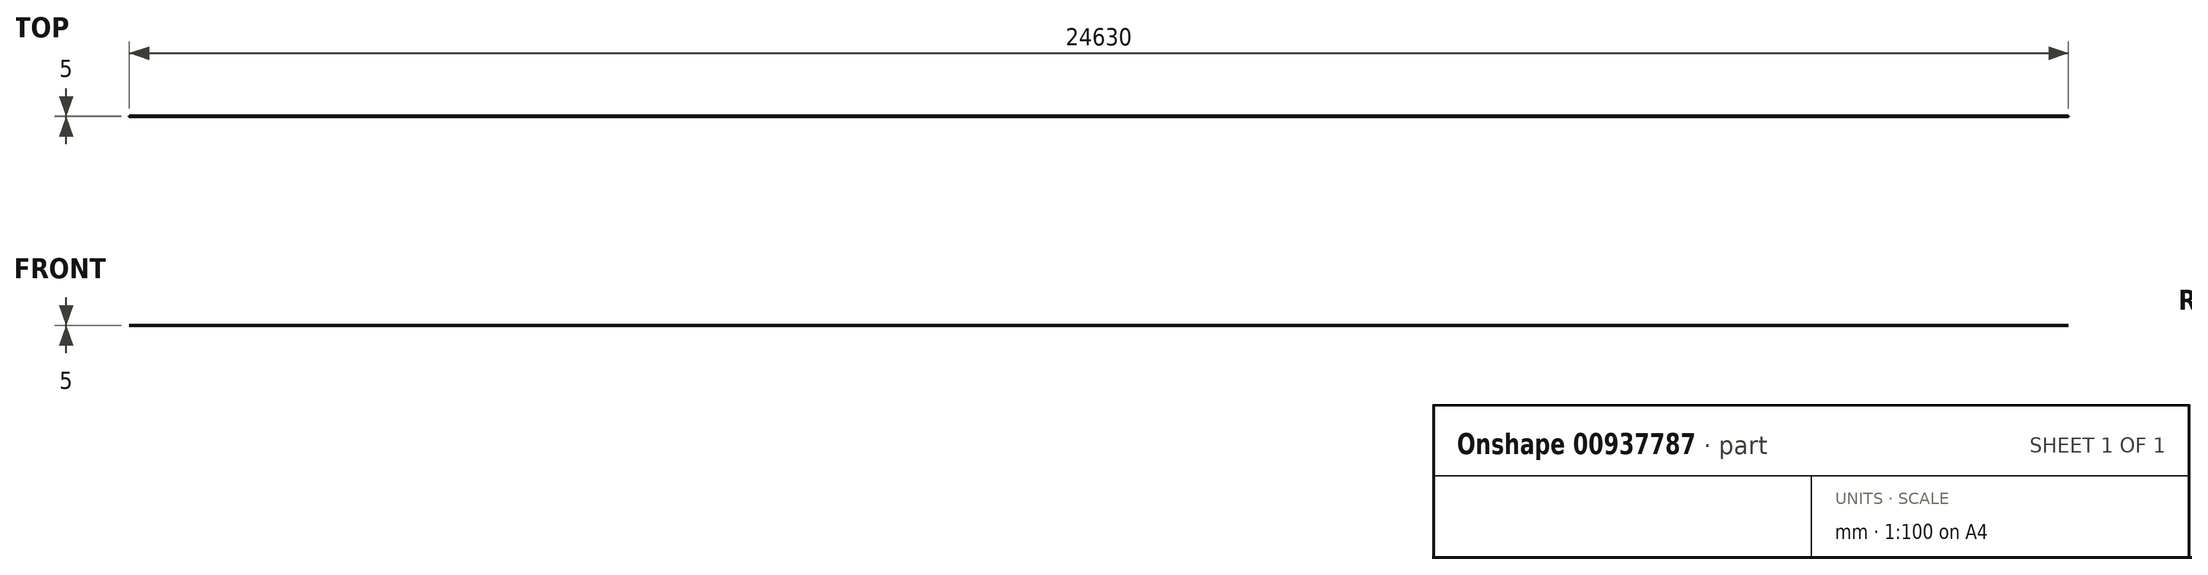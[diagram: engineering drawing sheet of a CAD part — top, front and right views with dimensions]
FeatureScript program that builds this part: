
annotation { "Feature Type Name" : "Feature", "Feature Type Description" : "" }
export const myFeature = defineFeature(function(context is Context, id is Id, definition is map)
    precondition{}
    {
        {
            var Q0;
            Q0=qCreatedBy(makeId("Right.planeOp"),FACE);
            var sketch = newSketch(context, id + "F0", { "sketchPlane" : qUnion([Q0])});
            skCircle(sketch, "E0", {"center": v(0, 0) * mm, "radius": 2.5 * mm});
            skSolve(sketch);
        }
        {
            var Q0;
            Q0=qSketchRegion(id+"F0",true);
            extrude(context, id + "F1", {"entities" : qUnion([Q0]), "depth" : 24590 * mm, "offsetDistance" : 25 * mm, "hasSecondDirection" : true, "secondDirectionOppositeDirection" : true, "secondDirectionDepth" : 40 * mm});
        }
    });
